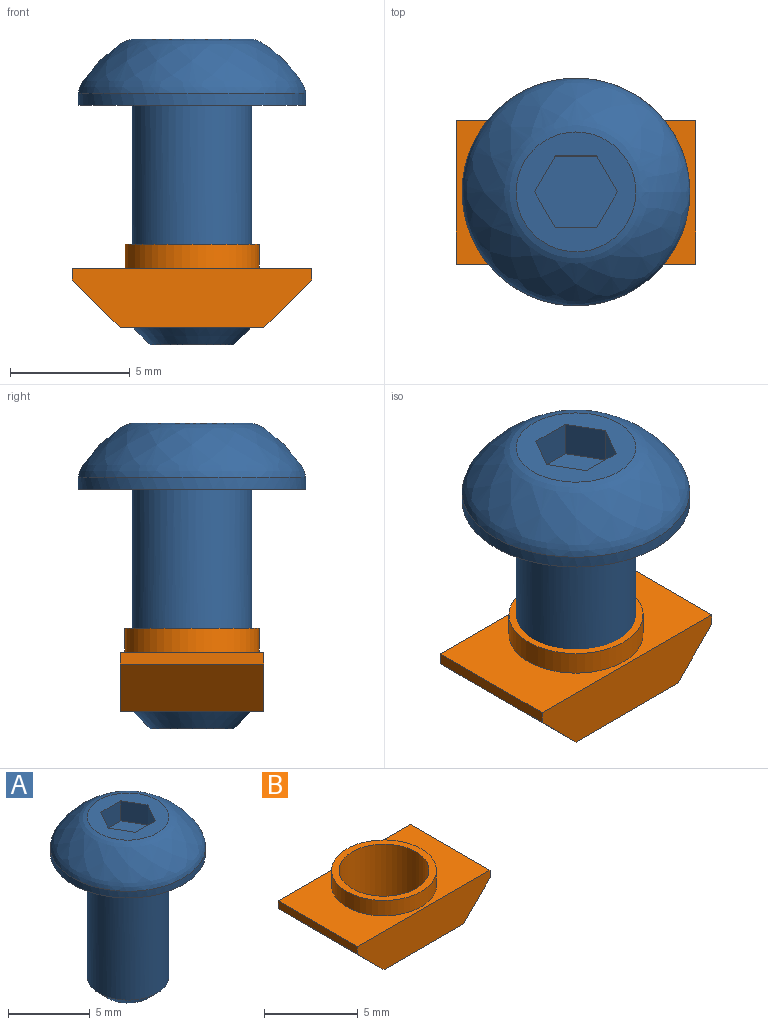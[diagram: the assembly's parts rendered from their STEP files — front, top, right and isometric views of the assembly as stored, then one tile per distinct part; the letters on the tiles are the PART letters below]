
ASSEMBLY  parts=2 mates=1
PART A: 14 faces, bbox 9.5x9.5x12.8 mm
  f0: plane 5.01x5.01mm, normal (0,0,1), area 11.8mm2, adj f3,f4,f5,f6,f7,f8,f10
  f1: cylinder r=4.75mm len=9.5mm, axis (0,0,-1), area 14.9mm2, adj f2,f10
  f2: plane 9.5x9.5mm, normal (0,0,-1), area 51.2mm2, adj f1,f11
  f3: plane 1.5x1.5mm, normal (-0.87,-0.5,0), area 2.6mm2, adj f0,f4,f8,f9
  f4: plane 1.73x1.5mm, normal (0,-1,0), area 2.6mm2, adj f0,f3,f5,f9
  f5: plane 1.5x1.5mm, normal (0.87,-0.5,0), area 2.6mm2, adj f0,f4,f6,f9
  f6: plane 1.5x1.5mm, normal (0.87,0.5,0), area 2.6mm2, adj f0,f5,f7,f9
  f7: plane 1.73x1.5mm, normal (0,1,0), area 2.6mm2, adj f0,f6,f8,f9
  f8: plane 1.5x1.5mm, normal (-0.87,0.5,0), area 2.6mm2, adj f0,f3,f7,f9
  f9: plane 3.46x3mm, normal (0,0,1), area 7.8mm2, adj f3,f4,f5,f6,f7,f8
  f10: bspline ~9.5x9.5mm, area 78.3mm2, adj f0,f1
  f11: cylinder r=2.5mm len=9.25mm, axis (0,0,1), area 145.3mm2, adj f2,f13
  f12: plane 3.5x3.5mm, normal (0,0,-1), area 9.6mm2, adj f13
  f13: cone r=1.75mm half-angle=45deg, axis (0,0,1), area 14.2mm2, adj f11,f12
PART B: 11 faces, bbox 10x6x3.5 mm
  f0: plane 10x2.5mm, normal (0,-1,0), area 21mm2, adj f1,f4,f5,f6,f9,f10
  f1: plane 6x0.5mm, normal (1,0,0), area 3mm2, adj f0,f2,f5,f10
  f2: plane 10x2.5mm, normal (0,1,0), area 21mm2, adj f1,f4,f5,f6,f9,f10
  f3: cylinder r=2.4mm len=4.8mm, axis (0,0,-1), area 52.8mm2, adj f6,f8
  f4: plane 6x0.5mm, normal (-1,0,0), area 3mm2, adj f0,f2,f5,f9
  f5: plane 10x6mm, normal (0,0,1), area 35.4mm2, adj f0,f1,f2,f4,f7
  f6: plane 6x6mm, normal (0,0,-1), area 17.9mm2, adj f0,f2,f3,f9,f10
  f7: cylinder r=2.8mm len=5.6mm, axis (0,0,-1), area 17.6mm2, adj f5,f8
  f8: plane 5.6x5.6mm, normal (0,0,1), area 6.5mm2, adj f3,f7
  f9: plane 6x2mm, normal (-0.71,0,-0.71), area 17mm2, adj f0,f2,f4,f6
  f10: plane 6x2mm, normal (0.71,0,-0.71), area 17mm2, adj f0,f1,f2,f6
PLACE A t=(2.85,-11.65,-10.35)mm
PLACE B t=(2.85,-11.65,-19.65)mm
MATE fastened B.f3 <-> A.f1  axis (0,0,1) through (2.85,-11.65,-17.15)mm
